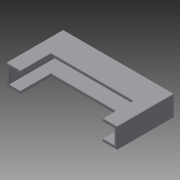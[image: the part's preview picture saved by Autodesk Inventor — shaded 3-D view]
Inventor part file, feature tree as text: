
AUTODESK INVENTOR PART (.ipt)
format: ipt  version: 2015 (Build 190159000, 159)  size: 169,472 bytes
history: native  units: mm
features: sketch x3, extrude x2, shell x1, hole x1, fillet x1
ambient origin geometry x8: Origin, YZ Plane, XZ Plane, XY Plane, X Axis, Y Axis, Z Axis, Center Point
bodies: Body1 (feature_tree)
feature tree (8):
  shell  "Shell1"  Thickness=68.8mm
  hole  "Hole1"  [1 undecoded]
  extrude  "Extrusion6"  Depth=15.0mm
  extrude  "Extrusion7"  Depth=2.0mm
  fillet  "Fillet1"  Radius=2.0mm
  sketch  "Sketch7"  dims[d13=33.0mm d14=7.5mm]
  sketch  "Sketch8"  dims[d15=7.5mm d16=15.0mm]
  sketch  "Sketch9"  dims[d17=9.5mm d18=0.0mm d19=2.0mm d26=2.0mm d28=2.0mm d29=6.0mm d30=6.0mm d31=2.0mm d32=90.0deg d33=8.0mm d34=20.594885mm d35=12.0mm d36=6.0mm d37=30.4mm d38=3.75mm d39=0.0mm d40=0.0mm d41=17.2mm d43=34.4mm d44=10.0mm d45=0.0mm d46=0.4mm]
note: 1 required parameter value undecoded (feature->parameter linkage not recoverable at this tier; creation-order binding heuristic only, values carry confidence <= 0.55)
